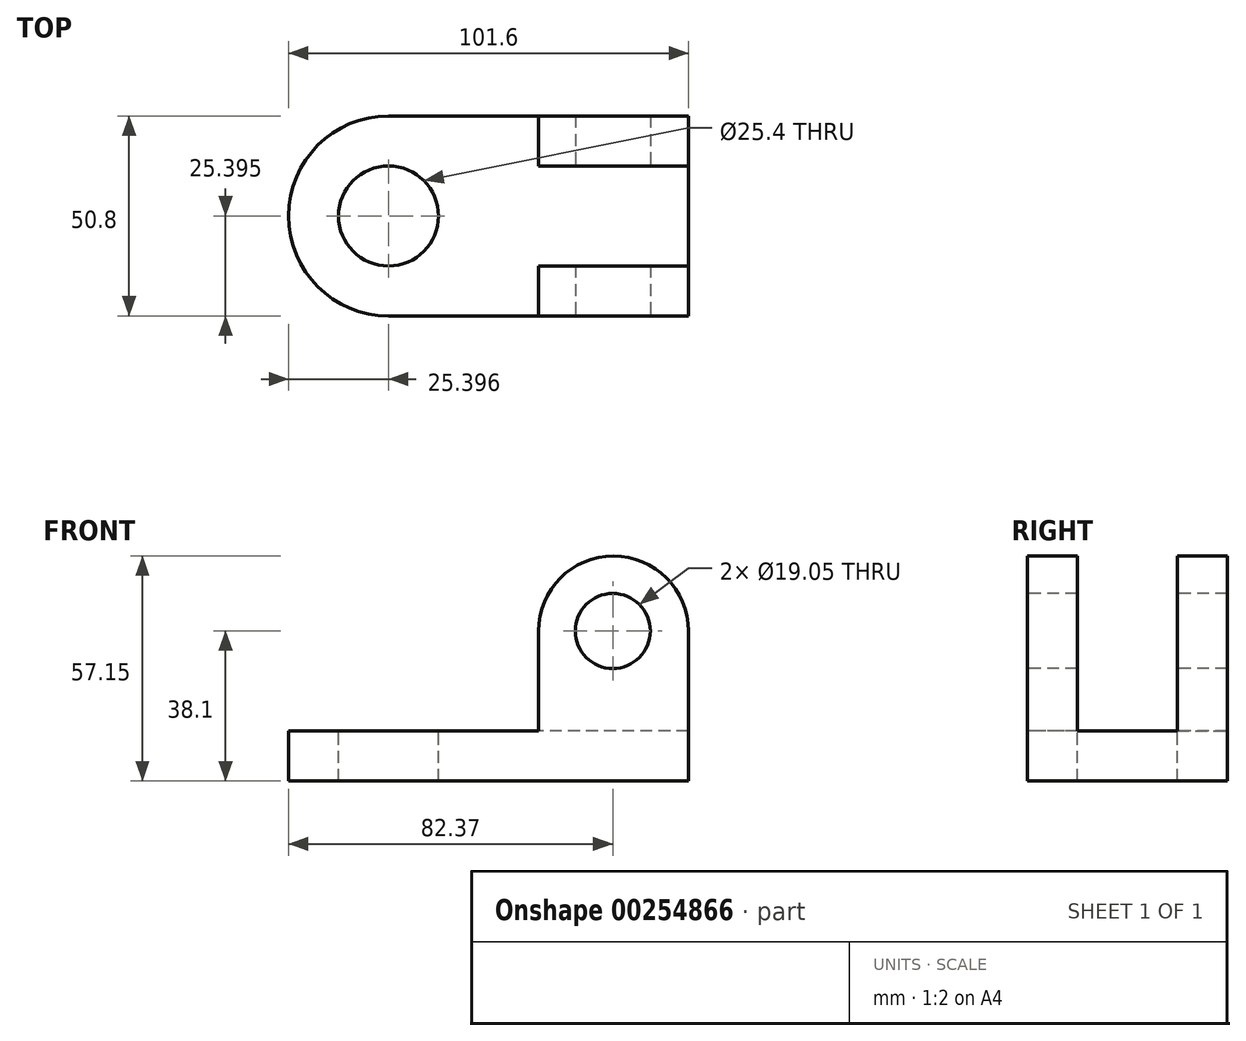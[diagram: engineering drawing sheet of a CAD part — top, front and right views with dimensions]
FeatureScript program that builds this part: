
annotation { "Feature Type Name" : "Feature", "Feature Type Description" : "" }
export const myFeature = defineFeature(function(context is Context, id is Id, definition is map)
    precondition{}
    {
        {
            var Q0;
            Q0=qCreatedBy(makeId("Top.planeOp"),FACE);
            var sketch = newSketch(context, id + "F0", { "sketchPlane" : qUnion([Q0])});
            skLineSegment(sketch, "E0", {"start": v(-48.06, -34.82) * mm, "end": v(53.54, -34.82) * mm});
            skLineSegment(sketch, "E1", {"start": v(53.54, -34.82) * mm, "end": v(53.54, 15.98) * mm});
            skLineSegment(sketch, "E2", {"start": v(53.54, 15.98) * mm, "end": v(-48.06, 15.98) * mm});
            skLineSegment(sketch, "E3", {"start": v(-48.06, 15.98) * mm, "end": v(-48.06, -34.82) * mm});
            skSolve(sketch);
        }
        {
            var Q0;
            Q0 = qSketchRegion(id + "F0", true);
            extrude(context, id + "F1", {"entities" : qUnion([Q0]), "depth" : 12.7 * mm});
        }
        {
            var Q0;
            Q0=makeQuery(id+"F1.opExtrude","SWEPT_EDGE",EDGE,{"disambiguationData":[OSD([sQuery(id+"F0.wireOp",EDGE,"E2"),sQuery(id+"F0.wireOp",EDGE,"E3")])]});
            var Q1;
            Q1=makeQuery(id+"F1.opExtrude","SWEPT_EDGE",EDGE,{"disambiguationData":[OSD([sQuery(id+"F0.wireOp",EDGE,"E0"),sQuery(id+"F0.wireOp",EDGE,"E3")])]});
            fillet(context, id + "F2", {"entities" : qUnion([Q0, Q1]), "radius" : 25.4 * mm, "tangentPropagation" : true, "allowEdgeOverflow" : false});
        }
        {
            var Q0;
            Q0=makeQuery(id+"F1.opExtrude","CAP_FACE",FACE,{"disambiguationData":[OSD([sQuery(id+"F0.wireOp",EDGE,"E0"),sQuery(id+"F0.wireOp",EDGE,"E1"),sQuery(id+"F0.wireOp",EDGE,"E2"),sQuery(id+"F0.wireOp",EDGE,"E3")])],"isStart":false});
            var sketch = newSketch(context, id + "F3", { "sketchPlane" : qUnion([Q0])});
            skCircle(sketch, "E4", {"center": v(-22.66, -9.42) * mm, "radius": 12.7 * mm});
            skSolve(sketch);
        }
        {
            var Q0;
            Q0 = qSketchRegion(id + "F3", true);
            extrude(context, id + "F4", {"entities" : qUnion([Q0]), "operationType" : NewBodyOperationType.REMOVE, "endBound" : BoundingType.THROUGH_ALL, "oppositeDirection" : true, "depth" : 25.4 * mm});
        }
        {
            var Q0;
            Q0=makeQuery(id+"F1.opExtrude","CAP_FACE",FACE,{"disambiguationData":[OSD([sQuery(id+"F0.wireOp",EDGE,"E0"),sQuery(id+"F0.wireOp",EDGE,"E1"),sQuery(id+"F0.wireOp",EDGE,"E2"),sQuery(id+"F0.wireOp",EDGE,"E3")])],"isStart":false});
            var sketch = newSketch(context, id + "F5", { "sketchPlane" : qUnion([Q0])});
            skLineSegment(sketch, "E5", {"start": v(53.54, -34.82) * mm, "end": v(53.54, -22.12) * mm});
            skLineSegment(sketch, "E6", {"start": v(53.54, -22.12) * mm, "end": v(15.44, -22.12) * mm});
            skLineSegment(sketch, "E7", {"start": v(15.44, -22.12) * mm, "end": v(15.44, -34.82) * mm});
            skLineSegment(sketch, "E8", {"start": v(15.44, -34.82) * mm, "end": v(53.54, -34.82) * mm});
            skSolve(sketch);
        }
        {
            var Q0;
            Q0=makeQuery(id+"F5.imprint","IMPRINT",FACE,{"disambiguationData":[TD([[makeQuery(id+"F5.imprint","IMPRINT",EDGE,{"derivedFrom":sQuery(id+"F5.wireOp",EDGE,"E5")}),1.0]])]});
            extrude(context, id + "F6", {"entities" : qUnion([Q0]), "operationType" : NewBodyOperationType.ADD, "depth" : 44.45 * mm});
        }
        {
            var Q0;
            Q0=makeQuery(id+"F6.opExtrude","CAP_EDGE",EDGE,{"disambiguationData":[OSD([sQuery(id+"F5.wireOp",EDGE,"E7")])],"isStart":false});
            var Q1;
            Q1=makeQuery(id+"F6.opExtrude","CAP_EDGE",EDGE,{"disambiguationData":[OSD([sQuery(id+"F5.wireOp",EDGE,"E5")])],"isStart":false});
            fillet(context, id + "F7", {"entities" : qUnion([Q0, Q1]), "radius" : 19.05 * mm, "tangentPropagation" : true, "allowEdgeOverflow" : false});
        }
        {
            var Q0;
            Q0=makeQuery(id+"F1.opExtrude","CAP_FACE",FACE,{"disambiguationData":[OSD([sQuery(id+"F0.wireOp",EDGE,"E0"),sQuery(id+"F0.wireOp",EDGE,"E1"),sQuery(id+"F0.wireOp",EDGE,"E2"),sQuery(id+"F0.wireOp",EDGE,"E3")])],"isStart":false});
            var sketch = newSketch(context, id + "F8", { "sketchPlane" : qUnion([Q0])});
            skLineSegment(sketch, "E9", {"start": v(53.54, 15.98) * mm, "end": v(53.54, 3.28) * mm});
            skLineSegment(sketch, "E10", {"start": v(53.54, 3.28) * mm, "end": v(15.44, 3.28) * mm});
            skLineSegment(sketch, "E11", {"start": v(15.44, 3.28) * mm, "end": v(15.44, 15.98) * mm});
            skLineSegment(sketch, "E12", {"start": v(15.44, 15.98) * mm, "end": v(53.54, 15.98) * mm});
            skSolve(sketch);
        }
        {
            var Q0;
            Q0=makeQuery(id+"F8.imprint","IMPRINT",FACE,{"disambiguationData":[TD([[makeQuery(id+"F8.imprint","IMPRINT",EDGE,{"derivedFrom":sQuery(id+"F8.wireOp",EDGE,"E9")}),1.0]])]});
            extrude(context, id + "F9", {"entities" : qUnion([Q0]), "operationType" : NewBodyOperationType.ADD, "depth" : 44.45 * mm});
        }
        {
            var Q0;
            Q0=makeQuery(id+"F9.opExtrude","CAP_EDGE",EDGE,{"disambiguationData":[OSD([sQuery(id+"F8.wireOp",EDGE,"E11")])],"isStart":false});
            var Q1;
            Q1=makeQuery(id+"F9.opExtrude","CAP_EDGE",EDGE,{"disambiguationData":[OSD([sQuery(id+"F8.wireOp",EDGE,"E9")])],"isStart":false});
            fillet(context, id + "F10", {"entities" : qUnion([Q0, Q1]), "radius" : 19.05 * mm, "tangentPropagation" : true, "allowEdgeOverflow" : false});
        }
        {
            var Q0;
            Q0=makeQuery(id+"F6.boolean.opBoolean","MERGE",FACE,{"derivedFrom":[makeQuery(id+"F1.opExtrude","SWEPT_FACE",FACE,{"disambiguationData":[OSD([sQuery(id+"F0.wireOp",EDGE,"E0")])]}),makeQuery(id+"F6.opExtrude","SWEPT_FACE",FACE,{"disambiguationData":[OSD([sQuery(id+"F5.wireOp",EDGE,"E8")])]})]});
            var sketch = newSketch(context, id + "F11", { "sketchPlane" : qUnion([Q0])});
            skCircle(sketch, "E13", {"center": v(34.3, 38.1) * mm, "radius": 9.53 * mm});
            skSolve(sketch);
        }
        {
            var Q0;
            Q0=makeQuery(id+"F11.imprint","IMPRINT",FACE,{"disambiguationData":[TD([[makeQuery(id+"F11.imprint","IMPRINT",EDGE,{"derivedFrom":sQuery(id+"F11.wireOp",EDGE,"E13")}),1.0]])]});
            extrude(context, id + "F12", {"entities" : qUnion([Q0]), "operationType" : NewBodyOperationType.REMOVE, "endBound" : BoundingType.THROUGH_ALL, "oppositeDirection" : true, "depth" : 25.4 * mm});
        }
    });
